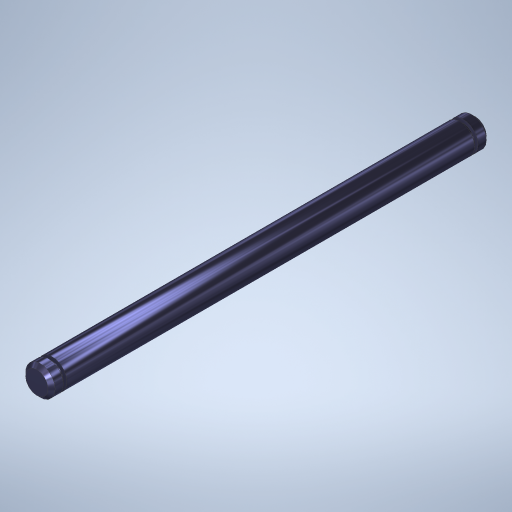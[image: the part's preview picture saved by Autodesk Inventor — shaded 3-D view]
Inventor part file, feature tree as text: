
AUTODESK INVENTOR PART (.ipt)
format: ipt  version: 2023.1 (Build 271208000, 208)  size: 295,424 bytes
history: native  units: in
note: dims shown in document units (in); Inventor stores cm internally (conversion verified against a paired STEP export)
features: extrude x3, sketch x3, chamfer x1, mirror x1
ambient origin geometry x8: Origin, YZ Plane, XZ Plane, XY Plane, X Axis, Y Axis, Z Axis, Center Point
bodies: Solid1 (feature_tree)
feature tree (8):
  extrude  "Extrusion1"  Depth=1.7238in TaperAngle=0.0deg
  extrude  "Extrusion2"  Depth=0.015in TaperAngle=0.0deg
  extrude  "Extrusion3"  Depth=0.015in TaperAngle=45.0deg
  chamfer  "Chamfer1"  [1 undecoded]
  mirror  "Mirror1"
  sketch  "Sketch1"  dims[d0=0.125in d1=1.7238in d2=0.0in]
  sketch  "Sketch2"  dims[d3=0.0938in d4=0.015in d5=0.0in]
  sketch  "Sketch3"  dims[d6=0.05in d7=0.0in d8=0.015in d9=0.125in d10=45.0deg]
note: 1 required parameter value undecoded (feature->parameter linkage not recoverable at this tier; creation-order binding heuristic only, values carry confidence <= 0.55)
